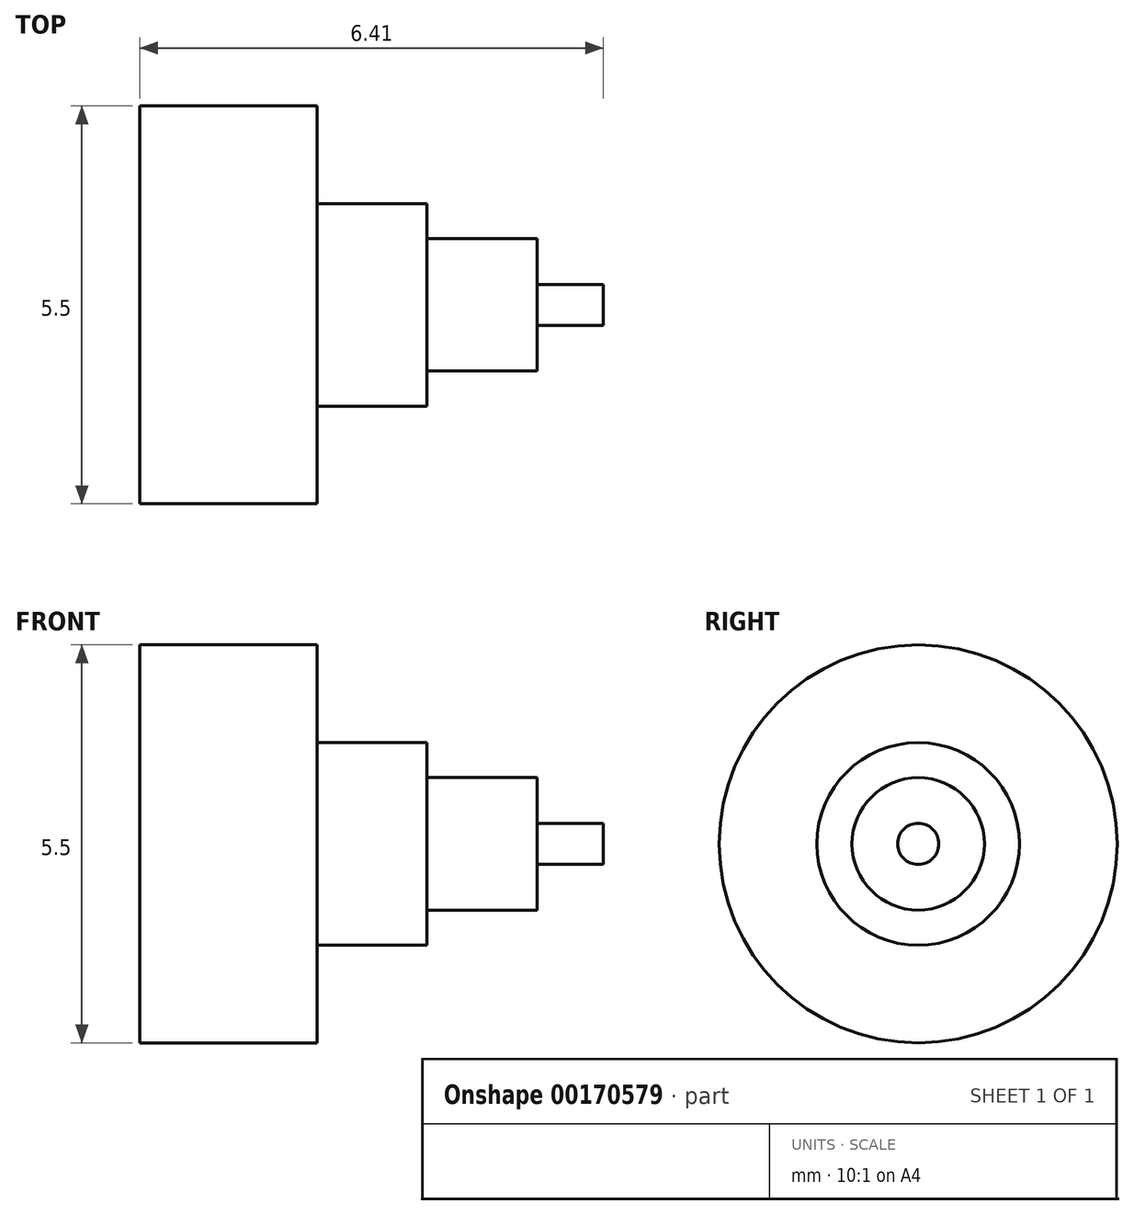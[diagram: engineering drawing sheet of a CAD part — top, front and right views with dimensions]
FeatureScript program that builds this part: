
annotation { "Feature Type Name" : "Feature", "Feature Type Description" : "" }
export const myFeature = defineFeature(function(context is Context, id is Id, definition is map)
    precondition{}
    {
        {
            var Q0;
            Q0=qCreatedBy(makeId("Right.planeOp"),FACE);
            var sketch = newSketch(context, id + "F0", { "sketchPlane" : qUnion([Q0])});
            skCircle(sketch, "E0", {"center": v(0, 0) * mm, "radius": 2.75 * mm});
            skSolve(sketch);
        }
        {
            var Q0;
            Q0 = qSketchRegion(id + "F0", true);
            extrude(context, id + "F1", {"entities" : qUnion([Q0]), "depth" : 2.45 * mm});
        }
        {
            var Q0;
            Q0=makeQuery(id+"F1.opExtrude","CAP_FACE",FACE,{"disambiguationData":[OSD([sQuery(id+"F0.wireOp",EDGE,"E0")])],"isStart":false});
            var sketch = newSketch(context, id + "F2", { "sketchPlane" : qUnion([Q0])});
            skCircle(sketch, "E1", {"center": v(0, 0) * mm, "radius": 1.4 * mm});
            skSolve(sketch);
        }
        {
            var Q0;
            Q0 = qSketchRegion(id + "F2", true);
            extrude(context, id + "F3", {"entities" : qUnion([Q0]), "operationType" : NewBodyOperationType.ADD, "depth" : 1.52 * mm});
        }
        {
            var Q0;
            Q0=makeQuery(id+"F3.opExtrude","CAP_FACE",FACE,{"disambiguationData":[OSD([sQuery(id+"F2.wireOp",EDGE,"E1")])],"isStart":false});
            var sketch = newSketch(context, id + "F4", { "sketchPlane" : qUnion([Q0])});
            skCircle(sketch, "E2", {"center": v(0, 0) * mm, "radius": 0.92 * mm});
            skSolve(sketch);
        }
        {
            var Q0;
            Q0 = qSketchRegion(id + "F4", true);
            extrude(context, id + "F5", {"entities" : qUnion([Q0]), "operationType" : NewBodyOperationType.ADD, "depth" : 1.52 * mm});
        }
        {
            var Q0;
            Q0=makeQuery(id+"F5.opExtrude","CAP_FACE",FACE,{"disambiguationData":[OSD([sQuery(id+"F4.wireOp",EDGE,"E2")])],"isStart":false});
            var sketch = newSketch(context, id + "F6", { "sketchPlane" : qUnion([Q0])});
            skCircle(sketch, "E3", {"center": v(0, 0) * mm, "radius": 0.28 * mm});
            skSolve(sketch);
        }
        {
            var Q0;
            Q0 = qSketchRegion(id + "F6", true);
            extrude(context, id + "F7", {"entities" : qUnion([Q0]), "operationType" : NewBodyOperationType.ADD, "depth" : 0.92 * mm});
        }
    });
